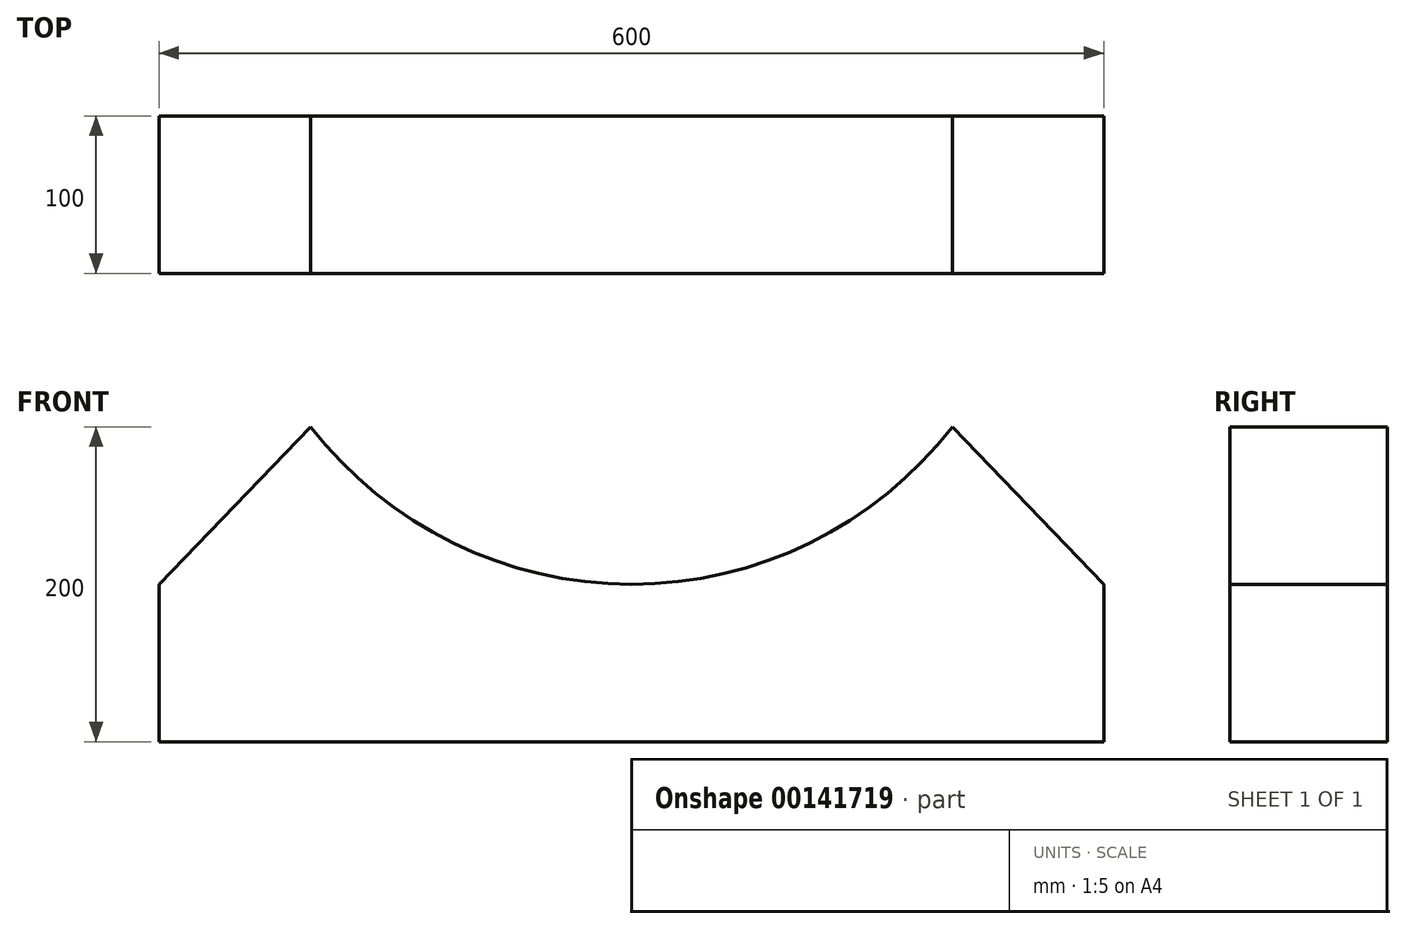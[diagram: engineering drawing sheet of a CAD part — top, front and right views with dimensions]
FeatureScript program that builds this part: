
annotation { "Feature Type Name" : "Feature", "Feature Type Description" : "" }
export const myFeature = defineFeature(function(context is Context, id is Id, definition is map)
    precondition{}
    {
        {
            var Q0;
            Q0=qCreatedBy(makeId("Front.planeOp"),FACE);
            var sketch = newSketch(context, id + "F0", { "sketchPlane" : qUnion([Q0])});
            skLineSegment(sketch, "E0", {"start": v(0, 0) * mm, "end": v(0, 341.45) * mm, "construction": true});
            skLineSegment(sketch, "E1", {"start": v(0, 100) * mm, "end": v(503.59, 100) * mm, "construction": true});
            skLineSegment(sketch, "E2", {"start": v(-300, 0) * mm, "end": v(300, 0) * mm});
            skLineSegment(sketch, "E3", {"start": v(300, 0) * mm, "end": v(300, 100) * mm});
            skLineSegment(sketch, "E4", {"start": v(-300, 0) * mm, "end": v(-300, 100) * mm});
            skLineSegment(sketch, "E5", {"start": v(-300, 100) * mm, "end": v(-203.72, 200) * mm});
            skLineSegment(sketch, "E6", {"start": v(300, 100) * mm, "end": v(203.72, 200) * mm});
            skArc(sketch, "E7", {"start": v(-203.72, 200) * mm, "mid": v(0, 100) * mm, "end": v(203.72, 200) * mm});
            skSolve(sketch);
        }
        {
            var Q0;
            Q0=makeQuery(id+"F0.imprint","IMPRINT",FACE,{"disambiguationData":[TD([[makeQuery(id+"F0.imprint","IMPRINT",EDGE,{"derivedFrom":sQuery(id+"F0.wireOp",EDGE,"E2")}),1.0]])]});
            extrude(context, id + "F1", {"entities" : qUnion([Q0]), "depth" : 100 * mm});
        }
    });
